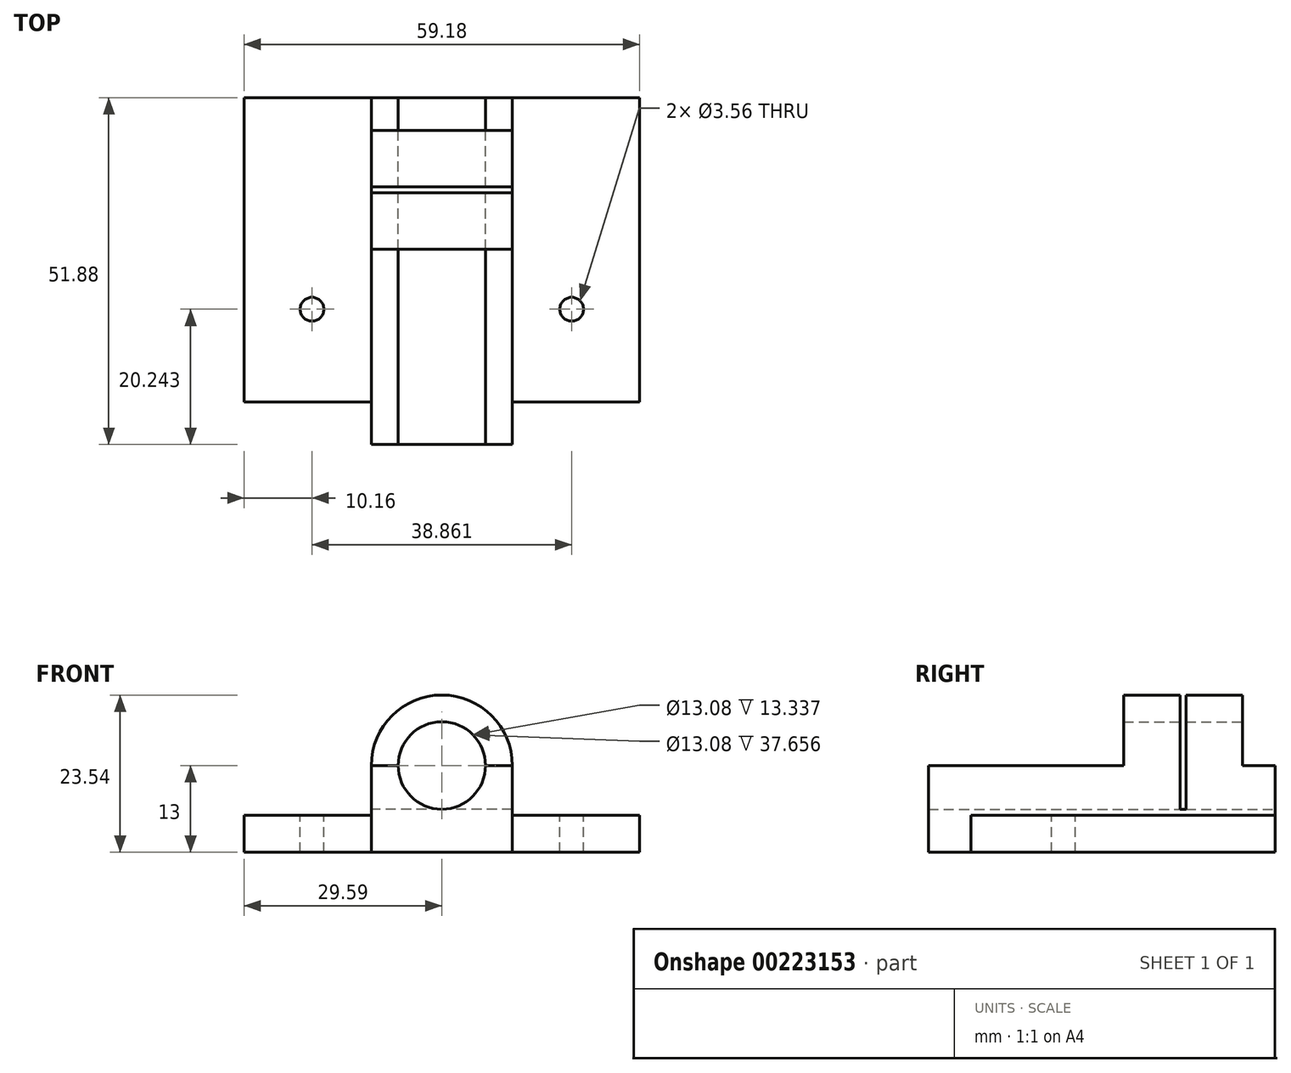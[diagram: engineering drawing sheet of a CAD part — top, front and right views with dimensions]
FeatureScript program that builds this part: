
annotation { "Feature Type Name" : "Feature", "Feature Type Description" : "" }
export const myFeature = defineFeature(function(context is Context, id is Id, definition is map)
    precondition{}
    {
        {
            var Q0;
            Q0=qCreatedBy(makeId("Front.planeOp"),FACE);
            var sketch = newSketch(context, id + "F0", { "sketchPlane" : qUnion([Q0])});
            skLineSegment(sketch, "E0", {"start": v(0, 0) * mm, "end": v(13.08, 0) * mm});
            skLineSegment(sketch, "E1", {"start": v(6.54, 0) * mm, "end": v(6.54, 6.54) * mm, "construction": true});
            skCircle(sketch, "E2", {"center": v(6.54, 6.54) * mm, "radius": 6.54 * mm});
            skCircle(sketch, "E3", {"center": v(6.54, 6.54) * mm, "radius": 10.54 * mm});
            skLineSegment(sketch, "E4", {"start": v(6.54, 6.54) * mm, "end": v(17.08, 6.54) * mm, "construction": true});
            skLineSegment(sketch, "E5", {"start": v(17.08, 6.54) * mm, "end": v(17.08, 0) * mm});
            skLineSegment(sketch, "E6", {"start": v(17.08, 0) * mm, "end": v(17.08, -3.46) * mm});
            skLineSegment(sketch, "E7", {"start": v(17.08, -3.46) * mm, "end": v(-4, -3.46) * mm});
            skLineSegment(sketch, "E8", {"start": v(6.54, 6.54) * mm, "end": v(-4, 6.54) * mm, "construction": true});
            skLineSegment(sketch, "E9", {"start": v(-4, 6.54) * mm, "end": v(-4, -3.46) * mm});
            skSolve(sketch);
        }
        {
            var Q0;
            Q0 = qSketchRegion(id + "F0", true);
            var Q1;
            {var subQ0=sQuery(id+"F0.wireOp",EDGE,"E0");var subQ1=makeQuery(id+"F0.imprint","INTERSECT",VERTEX,{"derivedFrom":[subQ0,sQuery(id+"F0.wireOp",EDGE,"E2")]});Q1=makeQuery(id+"F0.imprint","IMPRINT",FACE,{"disambiguationData":[TD([[makeQuery(id+"F0.imprint","IMPRINT",EDGE,{"disambiguationData":[TD([[subQ1,1.0]])],"derivedFrom":subQ0}),-1.0]])]});}
            extrude(context, id + "F1", {"entities" : qUnion([Q0, Q1]), "endBound" : BoundingType.SYMMETRIC, "depth" : 76.2 * mm});
        }
        {
            var Q0;
            Q0=qCreatedBy(makeId("Top.planeOp"),FACE);
            var sketch = newSketch(context, id + "F2", { "sketchPlane" : qUnion([Q0])});
            skLineSegment(sketch, "E10.bottom", {"start": v(23.37, -0.44) * mm, "end": v(-23.37, -0.44) * mm});
            skLineSegment(sketch, "E10.top", {"start": v(23.37, 0.44) * mm, "end": v(-23.37, 0.44) * mm});
            skLineSegment(sketch, "E10.left", {"start": v(23.37, -0.44) * mm, "end": v(23.37, 0.44) * mm});
            skLineSegment(sketch, "E10.right", {"start": v(-23.37, -0.44) * mm, "end": v(-23.37, 0.44) * mm});
            skPoint(sketch, "E10.middle", {"position": v(0, 0) * mm});
            skSolve(sketch);
        }
        {
            var Q0;
            Q0 = qSketchRegion(id + "F2", true);
            extrude(context, id + "F3", {"entities" : qUnion([Q0]), "operationType" : NewBodyOperationType.REMOVE, "depth" : 20.6 * mm});
        }
        {
            var Q0;
            Q0=makeQuery(id+"F1.opExtrude","CAP_FACE",FACE,{"disambiguationData":[OSD([sQuery(id+"F0.wireOp",EDGE,"E2"),sQuery(id+"F0.wireOp",EDGE,"E3"),sQuery(id+"F0.wireOp",EDGE,"E5"),sQuery(id+"F0.wireOp",EDGE,"E6"),sQuery(id+"F0.wireOp",EDGE,"E7"),sQuery(id+"F0.wireOp",EDGE,"E9")])],"isStart":true});
            var sketch = newSketch(context, id + "F4", { "sketchPlane" : qUnion([Q0])});
            skLineSegment(sketch, "E11", {"start": v(-17.08, 6.54) * mm, "end": v(4, 6.54) * mm});
            skLineSegment(sketch, "E12", {"start": v(3.58, 7.08) * mm, "end": v(4, 28.6) * mm});
            skLineSegment(sketch, "E13", {"start": v(4, 28.6) * mm, "end": v(-17.08, 29.01) * mm});
            skLineSegment(sketch, "E14", {"start": v(-17.6, 27.93) * mm, "end": v(-17.08, 6.54) * mm});
            skLineSegment(sketch, "E15", {"start": v(-17.6, 27.93) * mm, "end": v(-17.08, 29.01) * mm});
            skSolve(sketch);
        }
        {
            var Q0;
            Q0 = qSketchRegion(id + "F4", true);
            var Q1;
            {var subQ0=sQuery(id+"F4.wireOp",EDGE,"E13");Q1=makeQuery(id+"F4.imprint","IMPRINT",FACE,{"disambiguationData":[TD([[makeQuery(id+"F4.imprint","IMPRINT",EDGE,{"derivedFrom":subQ0}),1.0]])]});}
            var Q2;
            {var subQ0=sQuery(id+"F4.wireOp",EDGE,"E11");var subQ1=makeQuery(id+"F1.opExtrude","CAP_EDGE",EDGE,{"disambiguationData":[OSD([sQuery(id+"F0.wireOp",EDGE,"E2")])],"isStart":true});var subQ2=makeQuery(id+"F4.imprint","INTERSECT",VERTEX,{"disambiguationData":[OD(0.0)],"derivedFrom":[subQ1,subQ0]});Q2=makeQuery(id+"F4.imprint","IMPRINT",FACE,{"disambiguationData":[TD([[makeQuery(id+"F4.imprint","IMPRINT",EDGE,{"disambiguationData":[TD([[subQ2,-1.0]])],"derivedFrom":subQ0}),1.0]])]});}
            var Q3;
            {var subQ0=sQuery(id+"F4.wireOp",EDGE,"E11");var subQ5=makeQuery(id+"F1.opExtrude","CAP_EDGE",EDGE,{"disambiguationData":[OSD([sQuery(id+"F0.wireOp",EDGE,"E2")])],"isStart":true});var subQ7=makeQuery(id+"F4.imprint","INTERSECT",VERTEX,{"disambiguationData":[OD(0.0)],"derivedFrom":[subQ5,subQ0]});Q3=makeQuery(id+"F4.imprint","IMPRINT",FACE,{"disambiguationData":[TD([[makeQuery(id+"F4.imprint","IMPRINT",EDGE,{"disambiguationData":[TD([[subQ7,-1.0]])],"derivedFrom":subQ5}),1.0]])]});}
            extrude(context, id + "F5", {"entities" : qUnion([Q0, Q1, Q2, Q3]), "operationType" : NewBodyOperationType.REMOVE, "oppositeDirection" : true, "depth" : 29.2 * mm});
        }
        {
            var Q0;
            Q0=makeQuery(id+"F1.opExtrude","CAP_FACE",FACE,{"disambiguationData":[OSD([sQuery(id+"F0.wireOp",EDGE,"E2"),sQuery(id+"F0.wireOp",EDGE,"E3"),sQuery(id+"F0.wireOp",EDGE,"E5"),sQuery(id+"F0.wireOp",EDGE,"E6"),sQuery(id+"F0.wireOp",EDGE,"E7"),sQuery(id+"F0.wireOp",EDGE,"E9")])],"isStart":false});
            var sketch = newSketch(context, id + "F6", { "sketchPlane" : qUnion([Q0])});
            skLineSegment(sketch, "E16", {"start": v(-4, 6.54) * mm, "end": v(17.08, 6.54) * mm});
            skLineSegment(sketch, "E17", {"start": v(17.08, 6.54) * mm, "end": v(17.08, 23.18) * mm});
            skLineSegment(sketch, "E18", {"start": v(17.08, 23.18) * mm, "end": v(-4, 23.18) * mm});
            skLineSegment(sketch, "E19", {"start": v(-4.53, 22.96) * mm, "end": v(-4, 6.54) * mm});
            skSolve(sketch);
        }
        {
            var Q0;
            {var subQ1=makeQuery(id+"F1.opExtrude","CAP_EDGE",EDGE,{"disambiguationData":[OSD([sQuery(id+"F0.wireOp",EDGE,"E3")])],"isStart":false});Q0=makeQuery(id+"F6.imprint","IMPRINT",FACE,{"disambiguationData":[TD([[makeQuery(id+"F6.imprint","IMPRINT",EDGE,{"derivedFrom":subQ1}),1.0]])]});}
            extrude(context, id + "F7", {"entities" : qUnion([Q0]), "operationType" : NewBodyOperationType.REMOVE, "oppositeDirection" : true, "depth" : 29.2 * mm});
        }
        {
            var Q0;
            Q0=makeQuery(id+"F1.opExtrude","SWEPT_FACE",FACE,{"disambiguationData":[OSD([sQuery(id+"F0.wireOp",EDGE,"E7")])]});
            var sketch = newSketch(context, id + "F8", { "sketchPlane" : qUnion([Q0])});
            skLineSegment(sketch, "E20", {"start": v(13.48, 38.1) * mm, "end": v(13.48, -38.1) * mm});
            skLineSegment(sketch, "E21.bottom", {"start": v(36.13, -31.75) * mm, "end": v(-23.05, -31.75) * mm});
            skLineSegment(sketch, "E21.top", {"start": v(36.13, 31.75) * mm, "end": v(-23.05, 31.75) * mm});
            skLineSegment(sketch, "E21.left", {"start": v(36.13, -31.75) * mm, "end": v(36.13, 31.75) * mm});
            skLineSegment(sketch, "E21.right", {"start": v(-23.05, -31.75) * mm, "end": v(-23.05, 31.75) * mm});
            skPoint(sketch, "E21.middle", {"position": v(13.48, 0) * mm});
            skSolve(sketch);
        }
        {
            var Q0;
            Q0 = qSketchRegion(id + "F8", true);
            extrude(context, id + "F9", {"entities" : qUnion([Q0]), "operationType" : NewBodyOperationType.ADD, "oppositeDirection" : true, "depth" : 2.54 * mm});
        }
        {
            var Q0;
            Q0 = qSketchRegion(id + "F8", true);
            extrude(context, id + "F10", {"entities" : qUnion([Q0]), "operationType" : NewBodyOperationType.ADD, "depth" : 3 * mm});
        }
        {
            var Q0;
            Q0=makeQuery(id+"F10.opExtrude","CAP_FACE",FACE,{"disambiguationData":[OSD([sQuery(id+"F8.wireOp",EDGE,"E21.bottom"),sQuery(id+"F8.wireOp",EDGE,"E21.top"),sQuery(id+"F8.wireOp",EDGE,"E21.left"),sQuery(id+"F8.wireOp",EDGE,"E21.right")])],"isStart":false});
            var sketch = newSketch(context, id + "F11", { "sketchPlane" : qUnion([Q0])});
            skLineSegment(sketch, "E22.bottom", {"start": v(-30.04, -13.78) * mm, "end": v(58.13, -13.78) * mm});
            skLineSegment(sketch, "E22.top", {"start": v(-30.04, -67.86) * mm, "end": v(58.13, -67.86) * mm});
            skLineSegment(sketch, "E22.left", {"start": v(-30.04, -13.78) * mm, "end": v(-30.04, -67.86) * mm});
            skLineSegment(sketch, "E22.right", {"start": v(58.13, -13.78) * mm, "end": v(58.13, -67.86) * mm});
            skSolve(sketch);
        }
        {
            var Q0;
            {var subQ5=makeQuery(id+"F10.opExtrude","CAP_EDGE",EDGE,{"disambiguationData":[OSD([sQuery(id+"F8.wireOp",EDGE,"E21.bottom")])],"isStart":false});Q0=makeQuery(id+"F11.imprint","IMPRINT",FACE,{"disambiguationData":[TD([[makeQuery(id+"F11.imprint","IMPRINT",EDGE,{"derivedFrom":subQ5}),-1.0]])]});}
            var Q1;
            Q1=makeQuery(id+"F11.imprint","IMPRINT",FACE,{"disambiguationData":[TD([[makeQuery(id+"F11.imprint","IMPRINT",EDGE,{"derivedFrom":sQuery(id+"F11.wireOp",EDGE,"E22.top")}),1.0]])]});
            extrude(context, id + "F12", {"entities" : qUnion([Q0, Q1]), "operationType" : NewBodyOperationType.REMOVE, "oppositeDirection" : true, "depth" : 69.34 * mm});
        }
        {
            var Q0;
            {var subQ1=sQuery(id+"F8.wireOp",EDGE,"E21.top");var subQ4=sQuery(id+"F0.wireOp",EDGE,"E7");Q0=makeQuery(id+"F10.boolean.opBoolean","SPLIT",FACE,{"disambiguationData":[TD([makeQuery(id+"F9.opExtrude","SWEPT_FACE",FACE,{"disambiguationData":[OSD([subQ1])]})])],"derivedFrom":makeQuery(id+"F9.boolean.opBoolean","MERGE",FACE,{"derivedFrom":[makeQuery(id+"F1.opExtrude","SWEPT_FACE",FACE,{"disambiguationData":[OSD([subQ4])]}),makeQuery(id+"F9.opExtrude","CAP_FACE",FACE,{"disambiguationData":[OSD([sQuery(id+"F8.wireOp",EDGE,"E21.bottom"),subQ1,sQuery(id+"F8.wireOp",EDGE,"E21.left"),sQuery(id+"F8.wireOp",EDGE,"E21.right")])],"isStart":true})]})});}
            var sketch = newSketch(context, id + "F13", { "sketchPlane" : qUnion([Q0])});
            skLineSegment(sketch, "E23.bottom", {"start": v(17.08, 38.1) * mm, "end": v(-4, 38.1) * mm});
            skLineSegment(sketch, "E23.top", {"start": v(17.08, 31.75) * mm, "end": v(-4, 31.75) * mm});
            skLineSegment(sketch, "E23.left", {"start": v(17.08, 38.1) * mm, "end": v(17.08, 31.75) * mm});
            skLineSegment(sketch, "E23.right", {"start": v(-4, 38.1) * mm, "end": v(-4, 31.75) * mm});
            skSolve(sketch);
        }
        {
            var Q0;
            Q0 = qSketchRegion(id + "F13", true);
            var Q1;
            Q1=makeQuery(id+"F10.opExtrude","CAP_VERTEX",VERTEX,{"disambiguationData":[OSD([sQuery(id+"F8.wireOp",EDGE,"E21.top"),sQuery(id+"F8.wireOp",EDGE,"E21.left")])],"isStart":false});
            extrude(context, id + "F14", {"entities" : qUnion([Q0]), "operationType" : NewBodyOperationType.ADD, "endBound" : BoundingType.UP_TO_VERTEX, "endBoundEntityVertex" : qUnion([Q1]), "depth" : 25.4 * mm});
        }
        {
            var Q0;
            {var subQ0=sQuery(id+"F8.wireOp",EDGE,"E21.bottom");var subQ1=sQuery(id+"F8.wireOp",EDGE,"E21.top");var subQ2=sQuery(id+"F8.wireOp",EDGE,"E21.right");Q0=makeQuery(id+"F9.boolean.opBoolean","SPLIT",FACE,{"disambiguationData":[TD([makeQuery(id+"F1.opExtrude","SWEPT_FACE",FACE,{"disambiguationData":[OSD([sQuery(id+"F0.wireOp",EDGE,"E9")])]})])],"derivedFrom":makeQuery(id+"F9.opExtrude","CAP_FACE",FACE,{"disambiguationData":[OSD([subQ0,subQ1,sQuery(id+"F8.wireOp",EDGE,"E21.left"),subQ2])],"isStart":false})});}
            var sketch = newSketch(context, id + "F15", { "sketchPlane" : qUnion([Q0])});
            skCircle(sketch, "E24", {"center": v(-12.9, -17.86) * mm, "radius": 1.78 * mm});
            skCircle(sketch, "E25", {"center": v(25.97, -17.86) * mm, "radius": 1.78 * mm});
            skSolve(sketch);
        }
        {
            var Q0;
            Q0 = qSketchRegion(id + "F15", true);
            extrude(context, id + "F16", {"entities" : qUnion([Q0]), "operationType" : NewBodyOperationType.REMOVE, "oppositeDirection" : true, "depth" : 25.4 * mm});
        }
    });
